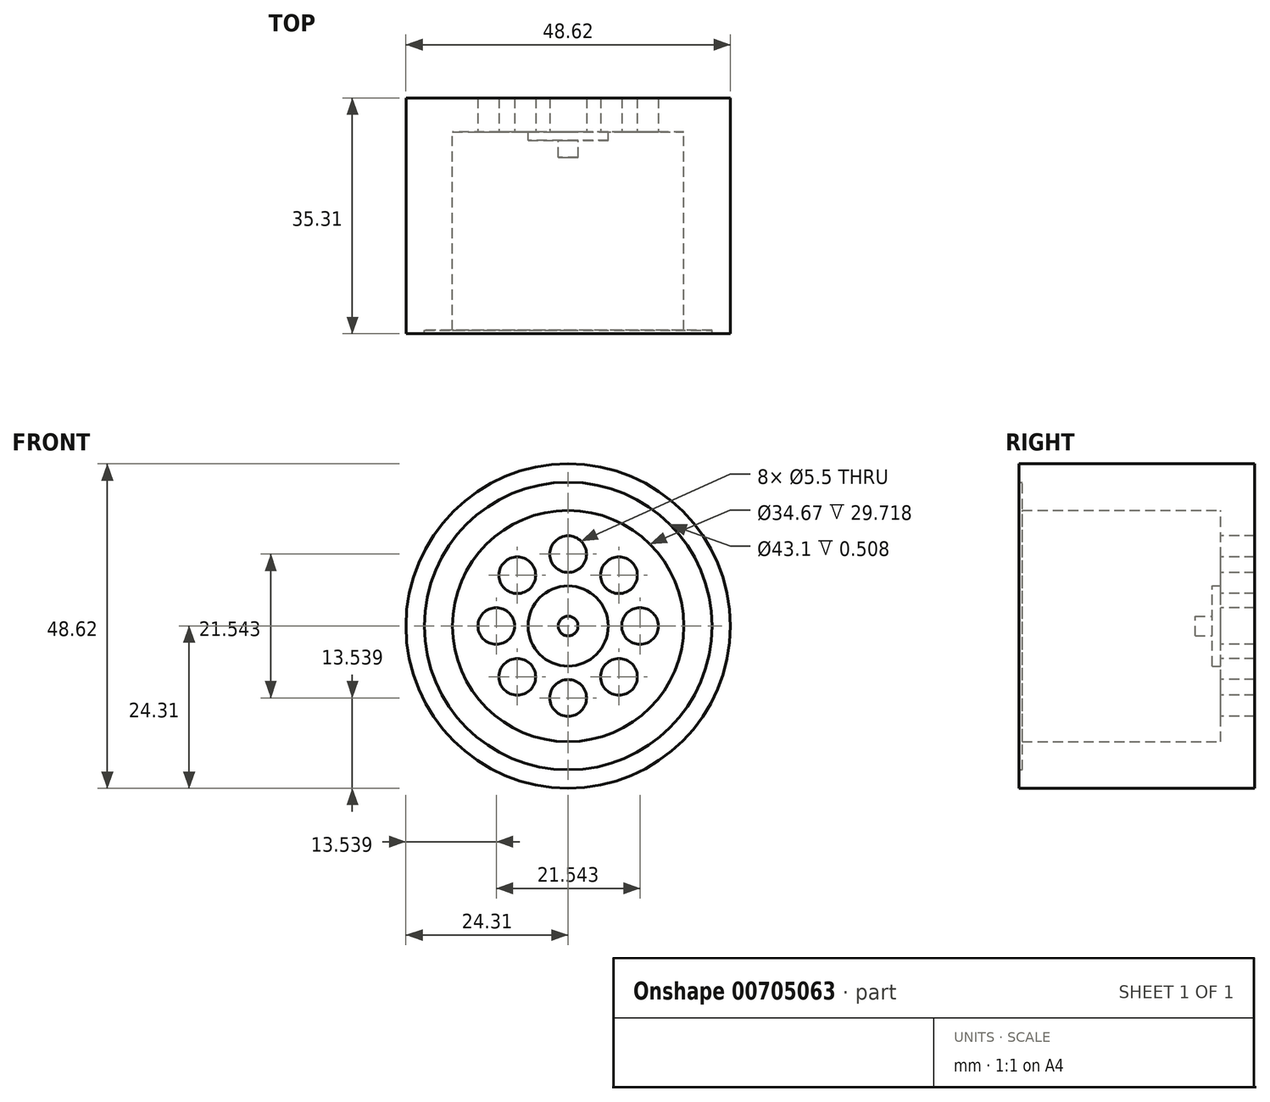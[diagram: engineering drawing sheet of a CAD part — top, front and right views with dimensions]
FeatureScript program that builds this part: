
annotation { "Feature Type Name" : "Feature", "Feature Type Description" : "" }
export const myFeature = defineFeature(function(context is Context, id is Id, definition is map)
    precondition{}
    {
        {
            var Q0;
            Q0=qCreatedBy(makeId("Front.planeOp"),FACE);
            var sketch = newSketch(context, id + "F0", { "sketchPlane" : qUnion([Q0])});
            skCircle(sketch, "E0", {"center": v(0, 0) * mm, "radius": 24.3 * mm});
            skSolve(sketch);
        }
        {
            var Q0;
            Q0=makeQuery(id+"F0.imprint","IMPRINT",FACE,{"disambiguationData":[TD([[makeQuery(id+"F0.imprint","IMPRINT",EDGE,{"derivedFrom":sQuery(id+"F0.wireOp",EDGE,"E0")}),1.0]])]});
            extrude(context, id + "F1", {"entities" : qUnion([Q0]), "depth" : 5.08 * mm, "offsetDistance" : 25.4 * mm});
        }
        {
            var Q0;
            Q0=makeQuery(id+"F1.opExtrude","CAP_FACE",FACE,{"disambiguationData":[OSD([sQuery(id+"F0.wireOp",EDGE,"E0")])],"isStart":false});
            var sketch = newSketch(context, id + "F2", { "sketchPlane" : qUnion([Q0])});
            skCircle(sketch, "E1", {"center": v(0, 0) * mm, "radius": 21.55 * mm});
            skSolve(sketch);
        }
        {
            var Q0;
            Q0=makeQuery(id+"F2.imprint","IMPRINT",FACE,{"disambiguationData":[TD([[makeQuery(id+"F2.imprint","IMPRINT",EDGE,{"derivedFrom":sQuery(id+"F2.wireOp",EDGE,"E1")}),1.0]])]});
            var sketch = newSketch(context, id + "F3", { "sketchPlane" : qUnion([Q0])});
            skCircle(sketch, "E2", {"center": v(0, 0) * mm, "radius": 6 * mm});
            skSolve(sketch);
        }
        {
            var Q0;
            Q0=makeQuery(id+"F2.imprint","IMPRINT",FACE,{"disambiguationData":[TD([[makeQuery(id+"F2.imprint","IMPRINT",EDGE,{"derivedFrom":sQuery(id+"F2.wireOp",EDGE,"E1")}),1.0]])]});
            var sketch = newSketch(context, id + "F4", { "sketchPlane" : qUnion([Q0])});
            skCircle(sketch, "E3", {"center": v(0, 0) * mm, "radius": 17.33 * mm});
            skSolve(sketch);
        }
        {
            var Q0;
            Q0=makeQuery(id+"F2.imprint","IMPRINT",FACE,{"disambiguationData":[TD([[makeQuery(id+"F2.imprint","IMPRINT",EDGE,{"derivedFrom":sQuery(id+"F2.wireOp",EDGE,"E1")}),-1.0]])]});
            extrude(context, id + "F5", {"entities" : qUnion([Q0]), "operationType" : NewBodyOperationType.ADD, "depth" : 2.3 * mm, "offsetDistance" : 25.4 * mm});
        }
        {
            var Q0;
            Q0=makeQuery(id+"F4.imprint","IMPRINT",FACE,{"disambiguationData":[TD([[makeQuery(id+"F4.imprint","IMPRINT",EDGE,{"derivedFrom":sQuery(id+"F4.wireOp",EDGE,"E3")}),-1.0]])]});
            extrude(context, id + "F6", {"entities" : qUnion([Q0]), "operationType" : NewBodyOperationType.ADD, "depth" : 1.78 * mm, "offsetDistance" : 25.4 * mm});
        }
        {
            var Q0;
            Q0=makeQuery(id+"F3.imprint","IMPRINT",FACE,{"disambiguationData":[TD([[makeQuery(id+"F3.imprint","IMPRINT",EDGE,{"derivedFrom":sQuery(id+"F3.wireOp",EDGE,"E2")}),1.0]])]});
            extrude(context, id + "F7", {"entities" : qUnion([Q0]), "operationType" : NewBodyOperationType.ADD, "depth" : 1.27 * mm, "offsetDistance" : 25.4 * mm});
        }
        {
            var Q0;
            Q0=makeQuery(id+"F7.opExtrude","CAP_FACE",FACE,{"disambiguationData":[OSD([sQuery(id+"F3.wireOp",EDGE,"E2")])],"isStart":false});
            var sketch = newSketch(context, id + "F8", { "sketchPlane" : qUnion([Q0])});
            skCircle(sketch, "E4", {"center": v(0, 0) * mm, "radius": 1.48 * mm});
            skSolve(sketch);
        }
        {
            var Q0;
            Q0=makeQuery(id+"F8.imprint","IMPRINT",FACE,{"disambiguationData":[TD([[makeQuery(id+"F8.imprint","IMPRINT",EDGE,{"derivedFrom":sQuery(id+"F8.wireOp",EDGE,"E4")}),1.0]])]});
            extrude(context, id + "F9", {"entities" : qUnion([Q0]), "operationType" : NewBodyOperationType.ADD, "depth" : 2.54 * mm, "offsetDistance" : 25.4 * mm});
        }
        {
            var Q0;
            Q0=makeQuery(id+"F1.opExtrude","CAP_FACE",FACE,{"disambiguationData":[OSD([sQuery(id+"F0.wireOp",EDGE,"E0")])],"isStart":false});
            var sketch = newSketch(context, id + "F10", { "sketchPlane" : qUnion([Q0])});
            skCircle(sketch, "E5", {"center": v(0, 10.77) * mm, "radius": 2.75 * mm});
            skCircle(sketch, "E6.1.0", {"center": v(-7.62, 7.62) * mm, "radius": 2.75 * mm});
            skCircle(sketch, "E6.2.0", {"center": v(-10.77, 0) * mm, "radius": 2.75 * mm});
            skCircle(sketch, "E6.3.0", {"center": v(-7.62, -7.62) * mm, "radius": 2.75 * mm});
            skCircle(sketch, "E6.4.0", {"center": v(0, -10.77) * mm, "radius": 2.75 * mm});
            skCircle(sketch, "E6.5.0", {"center": v(7.62, -7.62) * mm, "radius": 2.75 * mm});
            skCircle(sketch, "E6.6.0", {"center": v(10.77, 0) * mm, "radius": 2.75 * mm});
            skCircle(sketch, "E6.7.0", {"center": v(7.62, 7.62) * mm, "radius": 2.75 * mm});
            skPoint(sketch, "E6.center", {"position": v(0, 0) * mm});
            skSolve(sketch);
        }
        {
            var Q0;
            Q0=makeQuery(id+"F10.imprint","IMPRINT",FACE,{"disambiguationData":[TD([[makeQuery(id+"F10.imprint","IMPRINT",EDGE,{"derivedFrom":sQuery(id+"F10.wireOp",EDGE,"E5")}),1.0]])]});
            var Q1;
            Q1=makeQuery(id+"F10.imprint","IMPRINT",FACE,{"disambiguationData":[TD([[makeQuery(id+"F10.imprint","IMPRINT",EDGE,{"derivedFrom":sQuery(id+"F10.wireOp",EDGE,"E6.7.0")}),1.0]])]});
            var Q2;
            Q2=makeQuery(id+"F10.imprint","IMPRINT",FACE,{"disambiguationData":[TD([[makeQuery(id+"F10.imprint","IMPRINT",EDGE,{"derivedFrom":sQuery(id+"F10.wireOp",EDGE,"E6.6.0")}),1.0]])]});
            var Q3;
            Q3=makeQuery(id+"F10.imprint","IMPRINT",FACE,{"disambiguationData":[TD([[makeQuery(id+"F10.imprint","IMPRINT",EDGE,{"derivedFrom":sQuery(id+"F10.wireOp",EDGE,"E6.5.0")}),1.0]])]});
            var Q4;
            Q4=makeQuery(id+"F10.imprint","IMPRINT",FACE,{"disambiguationData":[TD([[makeQuery(id+"F10.imprint","IMPRINT",EDGE,{"derivedFrom":sQuery(id+"F10.wireOp",EDGE,"E6.4.0")}),1.0]])]});
            var Q5;
            Q5=makeQuery(id+"F10.imprint","IMPRINT",FACE,{"disambiguationData":[TD([[makeQuery(id+"F10.imprint","IMPRINT",EDGE,{"derivedFrom":sQuery(id+"F10.wireOp",EDGE,"E6.3.0")}),1.0]])]});
            var Q6;
            Q6=makeQuery(id+"F10.imprint","IMPRINT",FACE,{"disambiguationData":[TD([[makeQuery(id+"F10.imprint","IMPRINT",EDGE,{"derivedFrom":sQuery(id+"F10.wireOp",EDGE,"E6.2.0")}),1.0]])]});
            var Q7;
            Q7=makeQuery(id+"F10.imprint","IMPRINT",FACE,{"disambiguationData":[TD([[makeQuery(id+"F10.imprint","IMPRINT",EDGE,{"derivedFrom":sQuery(id+"F10.wireOp",EDGE,"E6.1.0")}),1.0]])]});
            extrude(context, id + "F11", {"entities" : qUnion([Q0, Q1, Q2, Q3, Q4, Q5, Q6, Q7]), "operationType" : NewBodyOperationType.REMOVE, "oppositeDirection" : true, "depth" : 25.4 * mm, "offsetDistance" : 25.4 * mm});
        }
        {
            var Q0;
            Q0=makeQuery(id+"F6.opExtrude","CAP_FACE",FACE,{"disambiguationData":[OSD([sQuery(id+"F2.wireOp",EDGE,"E1"),sQuery(id+"F4.wireOp",EDGE,"E3")])],"isStart":false});
            var Q1;
            Q1=makeQuery(id+"F5.opExtrude","CAP_FACE",FACE,{"disambiguationData":[OSD([sQuery(id+"F0.wireOp",EDGE,"E0"),sQuery(id+"F2.wireOp",EDGE,"E1")])],"isStart":false});
            extrude(context, id + "F12", {"entities" : qUnion([Q0, Q1]), "operationType" : NewBodyOperationType.ADD, "depth" : 27.94 * mm, "offsetDistance" : 25.4 * mm});
        }
    });
